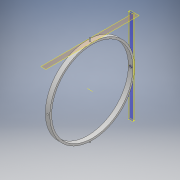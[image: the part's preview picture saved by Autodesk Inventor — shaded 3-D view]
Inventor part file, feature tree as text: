
AUTODESK INVENTOR PART (.ipt)
format: ipt  version: 2018 (Build 220112000, 112)  size: 164,352 bytes
history: native  units: mm
features: extrude x6, sketch x6, plane x4, other x1, mirror x1, projected_geometry x1
ambient origin geometry x8: Origin, YZ Plane, XZ Plane, XY Plane, X Axis, Y Axis, Z Axis, Center Point
bodies: Solid1 (feature_tree)
feature tree (19):
  extrude  "Extrusion1"  Depth=188.0mm
  plane  "Work Plane1"
  extrude  "Extrusion2"  Depth=10.0mm
  plane  "Work Plane2"
  extrude  "Extrusion3"  Depth=230.0mm TaperAngle=0.0deg
  plane  "Work Plane3"
  extrude  "Extrusion4"  Depth=2.5mm TaperAngle=0.0deg
  other  "Work Axis1"
  plane  "Work Plane4"
  extrude  "Extrusion5"  Depth=6.0mm
  mirror  "Mirror1"
  extrude  "Extrusion6"  Depth=3.0mm
  sketch  "Sketch1"  dims[d0=180.0mm d1=188.0mm]
  sketch  "Sketch2"  dims[d2=10.0mm d3=0.0mm d4=6.0mm]
  projected_geometry  "Projected Loop1"
  sketch  "Sketch3"  dims[d5=3.0mm d6=230.0mm d7=0.0mm]
  sketch  "Sketch4"  dims[d8=6.0mm d9=2.5mm d10=0.0mm]
  sketch  "Sketch5"  dims[d11=-4.0mm d12=6.0mm]
  sketch  "Sketch6"  dims[d13=2.5mm d14=0.0mm d15=3.0mm d16=12.0mm d17=0.0mm d18=8.0mm d19=0.0mm]
